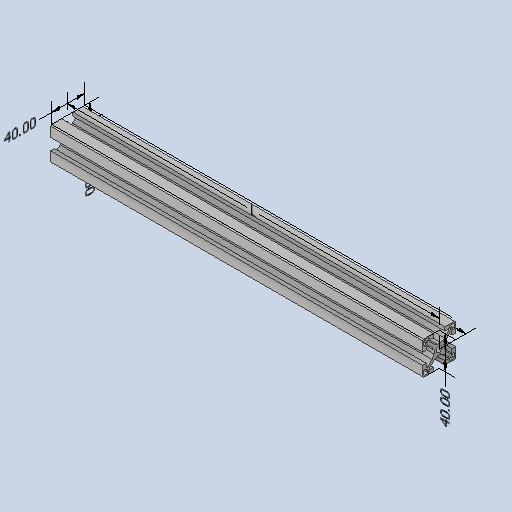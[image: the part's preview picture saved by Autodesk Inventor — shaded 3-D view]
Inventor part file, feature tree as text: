
AUTODESK INVENTOR PART (.ipt)
format: ipt  version: 2023 (Build 270158000, 158)  size: 278,016 bytes
history: native  units: mm
features: other x125, extrude x1, sketch x1
ambient origin geometry x8: Origin, YZ Plane, XZ Plane, XY Plane, X Axis, Y Axis, Z Axis, Center Point
bodies: Solid1 (feature_tree)
feature tree (127):
  other  "Annotations"
  extrude  "Extrusion1"  [1 undecoded]
  other  "CS_ANBAU_HINTEN_LINKS_XY"
  other  "CS_ANBAU_HINTEN_LINKS_YZ"
  other  "CS_ANBAU_HINTEN_LINKS_ZX"
  other  "CS_ANBAU_HINTEN_LINKS_X"
  other  "CS_ANBAU_HINTEN_LINKS_Y"
  other  "CS_ANBAU_HINTEN_LINKS_Z"
  other  "CS_ANBAU_HINTEN_LINKS_Center"
  other  "CS_ANBAU_HINTEN_OBEN_XY"
  other  "CS_ANBAU_HINTEN_OBEN_YZ"
  other  "CS_ANBAU_HINTEN_OBEN_ZX"
  other  "CS_ANBAU_HINTEN_OBEN_X"
  other  "CS_ANBAU_HINTEN_OBEN_Y"
  other  "CS_ANBAU_HINTEN_OBEN_Z"
  other  "CS_ANBAU_HINTEN_OBEN_Center"
  other  "CS_ANBAU_HINTEN_RECHTS_XY"
  other  "CS_ANBAU_HINTEN_RECHTS_YZ"
  other  "CS_ANBAU_HINTEN_RECHTS_ZX"
  other  "CS_ANBAU_HINTEN_RECHTS_X"
  other  "CS_ANBAU_HINTEN_RECHTS_Y"
  other  "CS_ANBAU_HINTEN_RECHTS_Z"
  other  "CS_ANBAU_HINTEN_RECHTS_Center"
  other  "CS_ANBAU_HINTEN_UNTEN_XY"
  other  "CS_ANBAU_HINTEN_UNTEN_YZ"
  other  "CS_ANBAU_HINTEN_UNTEN_ZX"
  other  "CS_ANBAU_HINTEN_UNTEN_X"
  other  "CS_ANBAU_HINTEN_UNTEN_Y"
  other  "CS_ANBAU_HINTEN_UNTEN_Z"
  other  "CS_ANBAU_HINTEN_UNTEN_Center"
  other  "CS_ANBAU_QUER_XY"
  other  "CS_ANBAU_QUER_YZ"
  other  "CS_ANBAU_QUER_ZX"
  other  "CS_ANBAU_QUER_X"
  other  "CS_ANBAU_QUER_Y"
  other  "CS_ANBAU_QUER_Z"
  other  "CS_ANBAU_QUER_Center"
  other  "CS_ANBAU_QUER_1_XY"
  other  "CS_ANBAU_QUER_1_YZ"
  other  "CS_ANBAU_QUER_1_ZX"
  other  "CS_ANBAU_QUER_1_X"
  other  "CS_ANBAU_QUER_1_Y"
  other  "CS_ANBAU_QUER_1_Z"
  other  "CS_ANBAU_QUER_1_Center"
  other  "CS_ANBAU_VORNE_LINKS_XY"
  other  "CS_ANBAU_VORNE_LINKS_YZ"
  other  "CS_ANBAU_VORNE_LINKS_ZX"
  other  "CS_ANBAU_VORNE_LINKS_X"
  other  "CS_ANBAU_VORNE_LINKS_Y"
  other  "CS_ANBAU_VORNE_LINKS_Z"
  other  "CS_ANBAU_VORNE_LINKS_Center"
  other  "CS_ANBAU_VORNE_OBEN_XY"
  other  "CS_ANBAU_VORNE_OBEN_YZ"
  other  "CS_ANBAU_VORNE_OBEN_ZX"
  other  "CS_ANBAU_VORNE_OBEN_X"
  other  "CS_ANBAU_VORNE_OBEN_Y"
  other  "CS_ANBAU_VORNE_OBEN_Z"
  other  "CS_ANBAU_VORNE_OBEN_Center"
  other  "CS_ANBAU_VORNE_RECHTS_XY"
  other  "CS_ANBAU_VORNE_RECHTS_YZ"
  other  "CS_ANBAU_VORNE_RECHTS_ZX"
  other  "CS_ANBAU_VORNE_RECHTS_X"
  other  "CS_ANBAU_VORNE_RECHTS_Y"
  other  "CS_ANBAU_VORNE_RECHTS_Z"
  other  "CS_ANBAU_VORNE_RECHTS_Center"
  other  "CS_ANBAU_VORNE_UNTEN_XY"
  other  "CS_ANBAU_VORNE_UNTEN_YZ"
  other  "CS_ANBAU_VORNE_UNTEN_ZX"
  other  "CS_ANBAU_VORNE_UNTEN_X"
  other  "CS_ANBAU_VORNE_UNTEN_Y"
  other  "CS_ANBAU_VORNE_UNTEN_Z"
  other  "CS_ANBAU_VORNE_UNTEN_Center"
  other  "p1_XY"
  other  "p1_YZ"
  other  "p1_ZX"
  other  "p1_X"
  other  "p1_Y"
  other  "p1_Z"
  other  "p1_Center"
  other  "p2_XY"
  other  "p2_YZ"
  other  "p2_ZX"
  other  "p2_X"
  other  "p2_Y"
  other  "p2_Z"
  other  "p2_Center"
  other  "p3_XY"
  other  "p3_YZ"
  other  "p3_ZX"
  other  "p3_X"
  other  "p3_Y"
  other  "p3_Z"
  other  "p3_Center"
  other  "p4_XY"
  other  "p4_YZ"
  other  "p4_ZX"
  other  "p4_X"
  other  "p4_Y"
  other  "p4_Z"
  other  "p4_Center"
  other  "p5_XY"
  other  "p5_YZ"
  other  "p5_ZX"
  other  "p5_X"
  other  "p5_Y"
  other  "p5_Z"
  other  "p5_Center"
  other  "pm1_XY"
  other  "pm1_YZ"
  other  "pm1_ZX"
  other  "pm1_X"
  other  "pm1_Y"
  other  "pm1_Z"
  other  "pm1_Center"
  other  "pm2_XY"
  other  "pm2_YZ"
  other  "pm2_ZX"
  other  "pm2_X"
  other  "pm2_Y"
  other  "pm2_Z"
  other  "pm2_Center"
  sketch  "Skizze_1"  dims[d0=450.0mm d1=0.0mm d2=0.0mm d3=0.0mm d4=0.0mm d5=0.0mm d6=0.0mm d10=450.0mm d11=450.0mm d7=40.0mm d8=40.0mm d9=40.0mm]
  other  "Linear Dimension 1"
  other  "Linear Dimension 2"
  other  "Linear Dimension 3"
  other  "Linear Dimension 4"
  other  "Linear Dimension 5"
note: 1 required parameter value undecoded (feature->parameter linkage not recoverable at this tier; creation-order binding heuristic only, values carry confidence <= 0.55)
